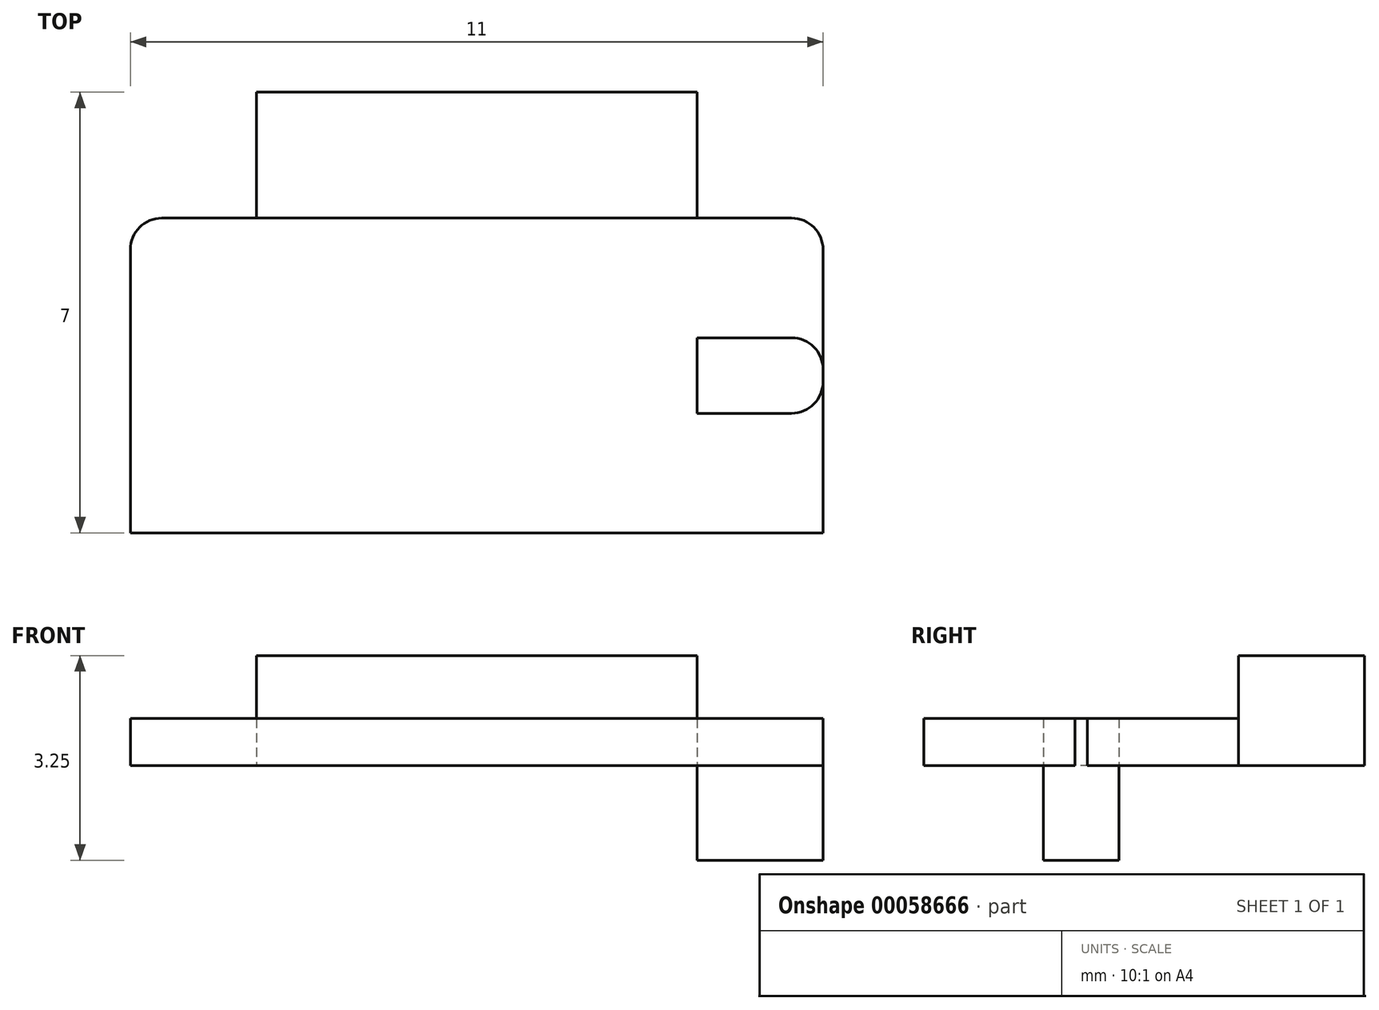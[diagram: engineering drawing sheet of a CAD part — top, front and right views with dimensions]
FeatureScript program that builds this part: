
annotation { "Feature Type Name" : "Feature", "Feature Type Description" : "" }
export const myFeature = defineFeature(function(context is Context, id is Id, definition is map)
    precondition{}
    {
        {
            var Q0;
            Q0=qCreatedBy(makeId("Top.planeOp"),FACE);
            var sketch = newSketch(context, id + "F0", { "sketchPlane" : qUnion([Q0])});
            skLineSegment(sketch, "E0.rect.bottom", {"start": v(3.5, 3.5) * mm, "end": v(-3.5, 3.5) * mm});
            skLineSegment(sketch, "E0.rect.top", {"start": v(3.5, -3.5) * mm, "end": v(-3.5, -3.5) * mm});
            skLineSegment(sketch, "E0.rect.left", {"start": v(3.5, 3.5) * mm, "end": v(3.5, -3.5) * mm});
            skLineSegment(sketch, "E0.rect.right", {"start": v(-3.5, 3.5) * mm, "end": v(-3.5, -3.5) * mm});
            skPoint(sketch, "E0.rect.middle", {"position": v(0, 0) * mm});
            skLineSegment(sketch, "E1.bottom", {"start": v(3.5, -3.5) * mm, "end": v(5.5, -3.5) * mm});
            skLineSegment(sketch, "E1.top", {"start": v(3.5, 1.5) * mm, "end": v(5, 1.5) * mm});
            skLineSegment(sketch, "E1.left", {"start": v(3.5, -3.5) * mm, "end": v(3.5, 1.5) * mm});
            skLineSegment(sketch, "E1.right", {"start": v(5.5, -3.5) * mm, "end": v(5.5, 1) * mm});
            skLineSegment(sketch, "E2.bottom", {"start": v(3.5, -1.6) * mm, "end": v(5, -1.6) * mm});
            skLineSegment(sketch, "E2.top", {"start": v(3.5, -0.4) * mm, "end": v(5, -0.4) * mm});
            skLineSegment(sketch, "E2.left", {"start": v(3.5, -1.6) * mm, "end": v(3.5, -0.4) * mm});
            skLineSegment(sketch, "E2.right", {"start": v(5.5, -1.1) * mm, "end": v(5.5, -0.9) * mm});
            skPoint(sketch, "E3.visualSharp", {"position": v(5.5, -0.4) * mm});
            skArc(sketch, "E3.filletArc", {"start": v(5.5, -0.9) * mm, "mid": v(5.35, -0.55) * mm, "end": v(5, -0.4) * mm});
            skPoint(sketch, "E4.visualSharp", {"position": v(5.5, -1.6) * mm});
            skArc(sketch, "E4.filletArc", {"start": v(5, -1.6) * mm, "mid": v(5.35, -1.45) * mm, "end": v(5.5, -1.1) * mm});
            skLineSegment(sketch, "E5.MirrorCS", {"start": v(-3.5, 1.5) * mm, "end": v(-5, 1.5) * mm});
            skLineSegment(sketch, "E6.MirrorCS", {"start": v(-5.5, -3.5) * mm, "end": v(-5.5, 1) * mm});
            skLineSegment(sketch, "E7.MirrorCS", {"start": v(-3.5, -3.5) * mm, "end": v(-5.5, -3.5) * mm});
            skPoint(sketch, "E8.visualSharp", {"position": v(5.5, 1.5) * mm});
            skArc(sketch, "E8.filletArc", {"start": v(5.5, 1) * mm, "mid": v(5.35, 1.35) * mm, "end": v(5, 1.5) * mm});
            skPoint(sketch, "E9.visualSharp", {"position": v(-5.5, 1.5) * mm});
            skArc(sketch, "E9.filletArc", {"start": v(-5, 1.5) * mm, "mid": v(-5.35, 1.35) * mm, "end": v(-5.5, 1) * mm});
            skLineSegment(sketch, "E10", {"start": v(-3.5, 1.5) * mm, "end": v(3.5, 1.5) * mm});
            skSolve(sketch);
        }
        {
            var Q0;
            {var subQ0=sQuery(id+"F0.wireOp",EDGE,"E5.MirrorCS");Q0=makeQuery(id+"F0.imprint","IMPRINT",FACE,{"disambiguationData":[TD([[makeQuery(id+"F0.imprint","IMPRINT",EDGE,{"derivedFrom":subQ0}),1.0]])]});}
            var Q1;
            {var subQ2=sQuery(id+"F0.wireOp",EDGE,"E1.bottom");Q1=makeQuery(id+"F0.imprint","IMPRINT",FACE,{"disambiguationData":[TD([[makeQuery(id+"F0.imprint","IMPRINT",EDGE,{"derivedFrom":subQ2}),1.0]])]});}
            var Q2;
            {var subQ5=sQuery(id+"F0.wireOp",EDGE,"E1.top");Q2=makeQuery(id+"F0.imprint","IMPRINT",FACE,{"disambiguationData":[TD([[makeQuery(id+"F0.imprint","IMPRINT",EDGE,{"derivedFrom":subQ5}),-1.0]])]});}
            var Q3;
            {var subQ3=sQuery(id+"F0.wireOp",EDGE,"E0.rect.top");Q3=makeQuery(id+"F0.imprint","IMPRINT",FACE,{"disambiguationData":[TD([[makeQuery(id+"F0.imprint","IMPRINT",EDGE,{"derivedFrom":subQ3}),-1.0]])]});}
            extrude(context, id + "F1", {"entities" : qUnion([Q0, Q1, Q2, Q3]), "depth" : 0.75 * mm});
        }
        {
            var Q0;
            Q0=makeQuery(id+"F0.imprint","IMPRINT",FACE,{"disambiguationData":[TD([[makeQuery(id+"F0.imprint","IMPRINT",EDGE,{"derivedFrom":sQuery(id+"F0.wireOp",EDGE,"E2.bottom")}),1.0]])]});
            extrude(context, id + "F2", {"entities" : qUnion([Q0]), "depth" : 0.75 * mm, "hasSecondDirection" : true, "secondDirectionOppositeDirection" : true, "secondDirectionDepth" : 1.5 * mm});
        }
        {
            var Q0;
            {var subQ0=sQuery(id+"F0.wireOp",EDGE,"E0.rect.bottom");Q0=makeQuery(id+"F0.imprint","IMPRINT",FACE,{"disambiguationData":[TD([[makeQuery(id+"F0.imprint","IMPRINT",EDGE,{"derivedFrom":subQ0}),1.0]])]});}
            extrude(context, id + "F3", {"entities" : qUnion([Q0]), "depth" : 1.75 * mm});
        }
    });
